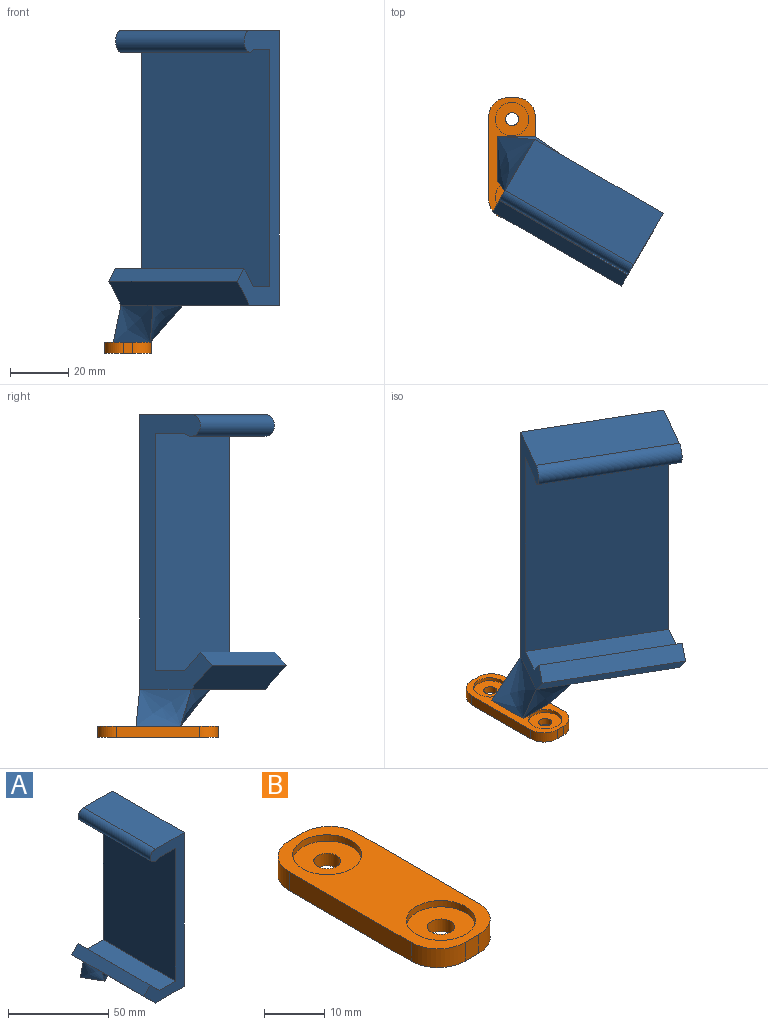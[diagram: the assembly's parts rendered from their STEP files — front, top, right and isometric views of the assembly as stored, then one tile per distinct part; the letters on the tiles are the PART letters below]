
ASSEMBLY  parts=2 mates=1
PART A: 17 faces, bbox 29.6x62.5x106.7 mm
  f0: plane 38.1x20.41mm, normal (0,0,-1), area 777.6mm2, adj f4,f5,f10,f15
  f1: plane 50.8x11.43mm, normal (0,0,1), area 580.6mm2, adj f2,f9,f10,f11
  f2: plane 50.8x6.35mm, normal (0.71,0,0.71), area 456.2mm2, adj f1,f3,f10,f11
  f3: plane 50.8x4.49mm, normal (-0.71,0,0.71), area 322.6mm2, adj f2,f4,f10,f11
  f4: plane 50.8x8.21mm, normal (-0.71,0,-0.71), area 589.8mm2, adj f0,f3,f10,f11,f14
  f5: plane 93.98x50.8mm, normal (1,0,0), area 4774.2mm2, adj f0,f6,f10,f11,f16
  f6: plane 50.8x20.32mm, normal (0,0,1), area 1032.3mm2, adj f5,f7,f10,f11
  f7: cylinder r=3.68mm len=50.8mm, axis (0,1,0), area 730.2mm2, adj f6,f8,f10,f11
  f8: plane 50.8x11.43mm, normal (0,0,-1), area 580.6mm2, adj f7,f9,f10,f11
  f9: plane 81.28x50.8mm, normal (-1,0,0), area 4129mm2, adj f1,f8,f10,f11
  f10: plane 93.98x28.62mm, normal (0,-1,0), area 854.9mm2, adj f0,f1,f2,f3,f4,f5,f6,f7
  f11: plane 93.98x28.62mm, normal (0,1,0), area 854.9mm2, adj f1,f2,f3,f4,f5,f6,f7,f8
  f12: plane 19.55x18.62mm, normal (0,0,-1), area 193.5mm2, adj f13,f14,f15,f16
  f13: bspline ~20.41x12.7mm, area 264.7mm2, adj f11,f12,f14,f16
  f14: bspline ~16.83x12.7mm, area 176.2mm2, adj f4,f12,f13,f15
  f15: bspline ~21.42x13.45mm, area 267.5mm2, adj f0,f12,f14,f16
  f16: bspline ~24.45x12.7mm, area 161.7mm2, adj f5,f12,f13,f15
PART B: 16 faces, bbox 15.9x41.3x3.8 mm
  f0: cylinder r=2.22mm len=4.45mm, axis (0,0,-1), area 35.5mm2, adj f11,f15
  f1: cylinder r=2.22mm len=4.45mm, axis (0,0,-1), area 35.5mm2, adj f11,f13
  f2: plane 28.58x3.81mm, normal (1,0,0), area 108.9mm2, adj f3,f9,f10,f11
  f3: cylinder r=6.35mm len=6.35mm, axis (0,0,-1), area 38mm2, adj f2,f4,f10,f11
  f4: plane 3.81x3.18mm, normal (0,1,0), area 12.1mm2, adj f3,f5,f10,f11
  f5: cylinder r=6.35mm len=6.35mm, axis (0,0,-1), area 38mm2, adj f4,f6,f10,f11
  f6: plane 28.58x3.81mm, normal (-1,0,0), area 108.9mm2, adj f5,f7,f10,f11
  f7: cylinder r=6.35mm len=6.35mm, axis (0,0,-1), area 38mm2, adj f6,f8,f10,f11
  f8: plane 3.81x3.18mm, normal (0,-1,0), area 12.1mm2, adj f7,f9,f10,f11
  f9: cylinder r=6.35mm len=6.35mm, axis (0,0,-1), area 38mm2, adj f2,f8,f10,f11
  f10: plane 41.28x15.88mm, normal (0,0,1), area 415.4mm2, adj f2,f3,f4,f5,f6,f7,f8,f9
  f11: plane 41.28x15.88mm, normal (0,0,-1), area 589.6mm2, adj f0,f1,f2,f3,f4,f5,f6,f7
  f12: cylinder r=5.71mm len=11.43mm, axis (0,0,1), area 45.6mm2, adj f10,f13
  f13: plane 11.43x11.43mm, normal (0,0,1), area 87.1mm2, adj f1,f12
  f14: cylinder r=5.71mm len=11.43mm, axis (0,0,1), area 45.6mm2, adj f10,f15
  f15: plane 11.43x11.43mm, normal (0,0,1), area 87.1mm2, adj f0,f14
PLACE A rot(axis=(0,0,1),60deg) t=(4.6,0.81,26.68)mm
PLACE B t=(0,0,3.82)mm
MATE planar A.f12 <-> B.f10  axis (0,0,-1) through (1.28,-0.07,7.63)mm
